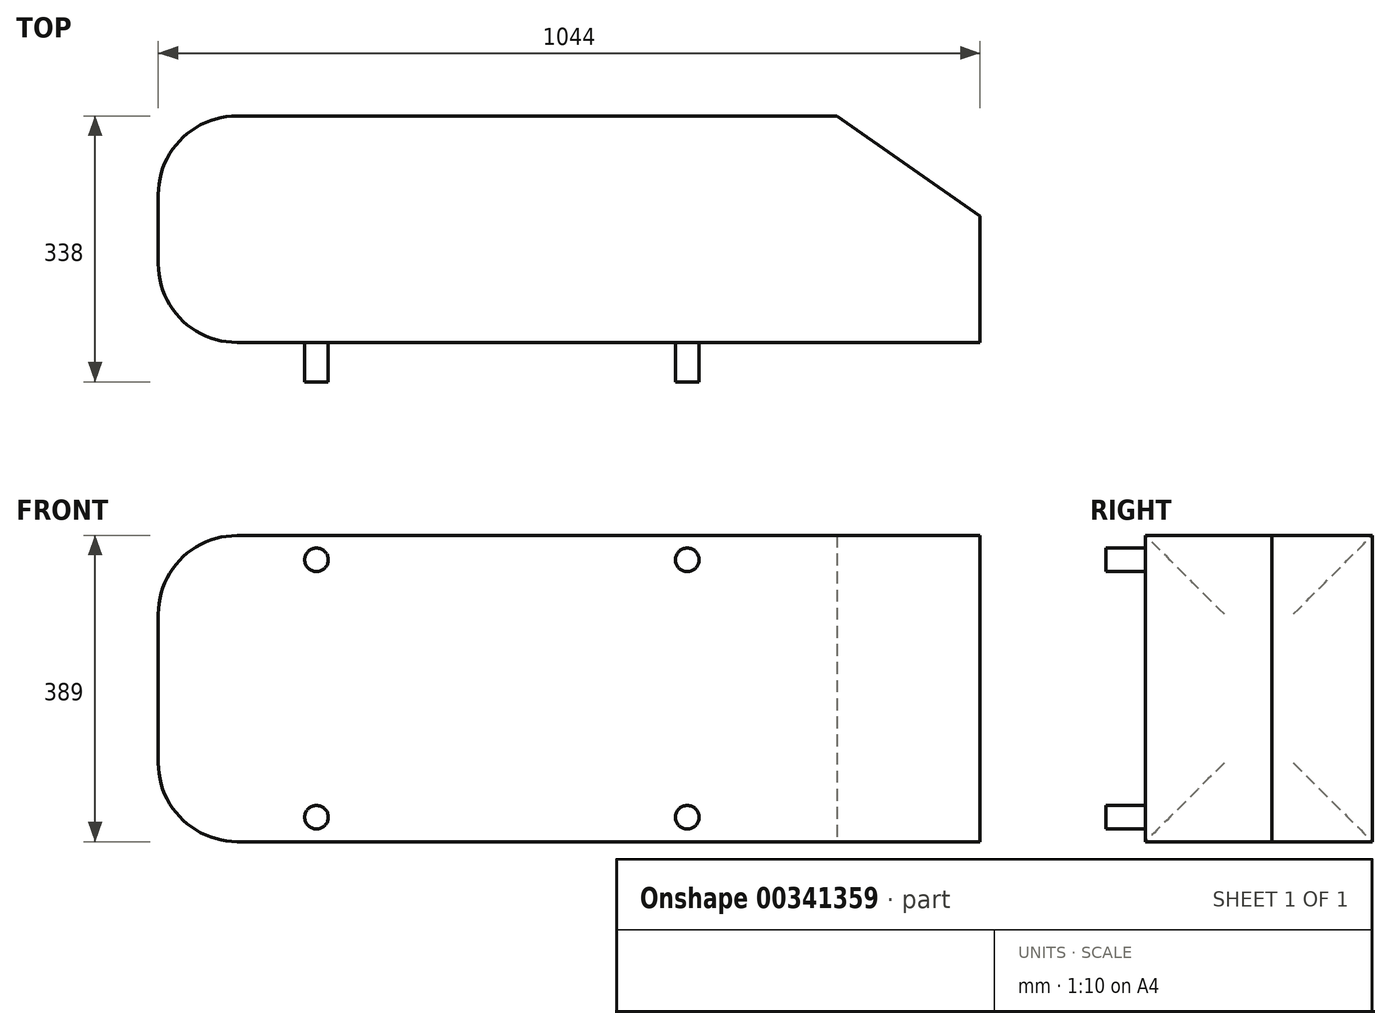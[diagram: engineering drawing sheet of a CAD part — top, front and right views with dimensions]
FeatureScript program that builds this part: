
annotation { "Feature Type Name" : "Feature", "Feature Type Description" : "" }
export const myFeature = defineFeature(function(context is Context, id is Id, definition is map)
    precondition{}
    {
        {
            var Q0;
            Q0=qCreatedBy(makeId("Top.planeOp"),FACE);
            var sketch = newSketch(context, id + "F0", { "sketchPlane" : qUnion([Q0])});
            skLineSegment(sketch, "E0", {"start": v(0, 0) * mm, "end": v(0, 50) * mm, "construction": true});
            skLineSegment(sketch, "E1", {"start": v(-378.78, 475.9) * mm, "end": v(90.55, 147.26) * mm, "construction": true});
            skLineSegment(sketch, "E2", {"start": v(0, 50) * mm, "end": v(-1044, 50) * mm});
            skLineSegment(sketch, "E3", {"start": v(0, 50) * mm, "end": v(0, 338) * mm, "construction": true});
            skLineSegment(sketch, "E4", {"start": v(0, 338) * mm, "end": v(-1044, 338) * mm, "construction": true});
            skLineSegment(sketch, "E5", {"start": v(-1044, 50) * mm, "end": v(-1044, 338) * mm});
            skLineSegment(sketch, "E6", {"start": v(0, 210.67) * mm, "end": v(-181.85, 338) * mm});
            skLineSegment(sketch, "E7", {"start": v(0, 50) * mm, "end": v(0, 210.67) * mm});
            skLineSegment(sketch, "E8", {"start": v(-1044, 338) * mm, "end": v(-181.85, 338) * mm});
            skSolve(sketch);
        }
        {
            var Q0;
            Q0 = qSketchRegion(id + "F0", true);
            extrude(context, id + "F1", {"entities" : qUnion([Q0]), "depth" : 194.5 * mm});
        }
        {
            var Q0;
            Q0 = qSketchRegion(id + "F0", true);
            extrude(context, id + "F2", {"entities" : qUnion([Q0]), "operationType" : NewBodyOperationType.ADD, "oppositeDirection" : true, "depth" : 194.5 * mm});
        }
        {
            var Q0;
            Q0=qCreatedBy(makeId("Front.planeOp"),FACE);
            var sketch = newSketch(context, id + "F3", { "sketchPlane" : qUnion([Q0])});
            skLineSegment(sketch, "E9", {"start": v(0, 0) * mm, "end": v(-372, 0) * mm, "construction": true});
            skLineSegment(sketch, "E10", {"start": v(-372, 0) * mm, "end": v(-843, 0) * mm, "construction": true});
            skLineSegment(sketch, "E11", {"start": v(-372, 0) * mm, "end": v(-372, 163.5) * mm, "construction": true});
            skLineSegment(sketch, "E12", {"start": v(-372, 0) * mm, "end": v(-372, -163.5) * mm, "construction": true});
            skLineSegment(sketch, "E13", {"start": v(-843, 0) * mm, "end": v(-843, 163.5) * mm, "construction": true});
            skLineSegment(sketch, "E14", {"start": v(-843, 0) * mm, "end": v(-843, -163.5) * mm, "construction": true});
            skCircle(sketch, "E15", {"center": v(-843, 163.5) * mm, "radius": 15 * mm});
            skCircle(sketch, "E16.MirrorC", {"center": v(-843, -163.5) * mm, "radius": 15 * mm});
            skCircle(sketch, "E17", {"center": v(-372, -163.5) * mm, "radius": 15 * mm});
            skCircle(sketch, "E18.MirrorC", {"center": v(-372, 163.5) * mm, "radius": 15 * mm});
            skSolve(sketch);
        }
        {
            var Q0;
            Q0 = qSketchRegion(id + "F3", true);
            extrude(context, id + "F4", {"entities" : qUnion([Q0]), "operationType" : NewBodyOperationType.ADD, "endBound" : BoundingType.UP_TO_NEXT, "oppositeDirection" : true, "depth" : 25 * mm});
        }
        {
            var Q0;
            {var subQ0=sQuery(id+"F0.wireOp",EDGE,"E5");Q0=makeQuery(id+"F2.boolean.opBoolean","MERGE",FACE,{"derivedFrom":[makeQuery(id+"F1.opExtrude","SWEPT_FACE",FACE,{"disambiguationData":[OSD([subQ0])]}),makeQuery(id+"F2.opExtrude","SWEPT_FACE",FACE,{"disambiguationData":[OSD([subQ0])]})]});}
            fillet(context, id + "F5", {"entities" : qUnion([Q0]), "radius" : 100 * mm, "tangentPropagation" : true, "allowEdgeOverflow" : false});
        }
    });
